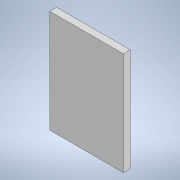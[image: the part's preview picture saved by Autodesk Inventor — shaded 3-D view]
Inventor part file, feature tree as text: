
AUTODESK INVENTOR PART (.ipt)
format: ipt  version: 2022.2 (Build 262287030, 287C)  size: 90,112 bytes
history: native  units: in
note: dims shown in document units (in); Inventor stores cm internally (conversion verified against a paired STEP export)
features: extrude x1, sketch x1
ambient origin geometry x8: Origin, YZ Plane, XZ Plane, XY Plane, X Axis, Y Axis, Z Axis, Center Point
bodies: Solid1 (feature_tree)
feature tree (2):
  extrude  "Extrusion1"  Depth=4.1339in
  sketch  "Sketch1"  dims[d0=2.9528in d1=4.1339in d2=0.2756in d3=0.0in]
